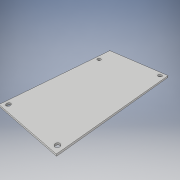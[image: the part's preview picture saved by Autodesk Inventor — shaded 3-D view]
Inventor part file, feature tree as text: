
AUTODESK INVENTOR PART (.ipt)
format: ipt  version: 2019 (Build 230136000, 136)  size: 105,472 bytes
history: native  units: mm
features: extrude x1, sketch x1
ambient origin geometry x8: Origin, YZ Plane, XZ Plane, XY Plane, X Axis, Y Axis, Z Axis, Center Point
bodies: Solid1 (feature_tree)
feature tree (2):
  extrude  "Extrusion1"  Depth=10.0mm
  sketch  "Sketch1"  dims[d0=3.5mm d1=20.0mm d3=46.16mm d4=10.0mm d6=10.0mm d8=20.0mm d10=92.0mm d11=10.0mm d13=10.0mm d15=20.0mm d17=79.0mm d18=10.0mm d20=10.0mm d22=4.0mm d23=4.0mm d24=4.0mm d25=4.0mm d26=4.0mm d27=1.6mm d28=0.0mm]
